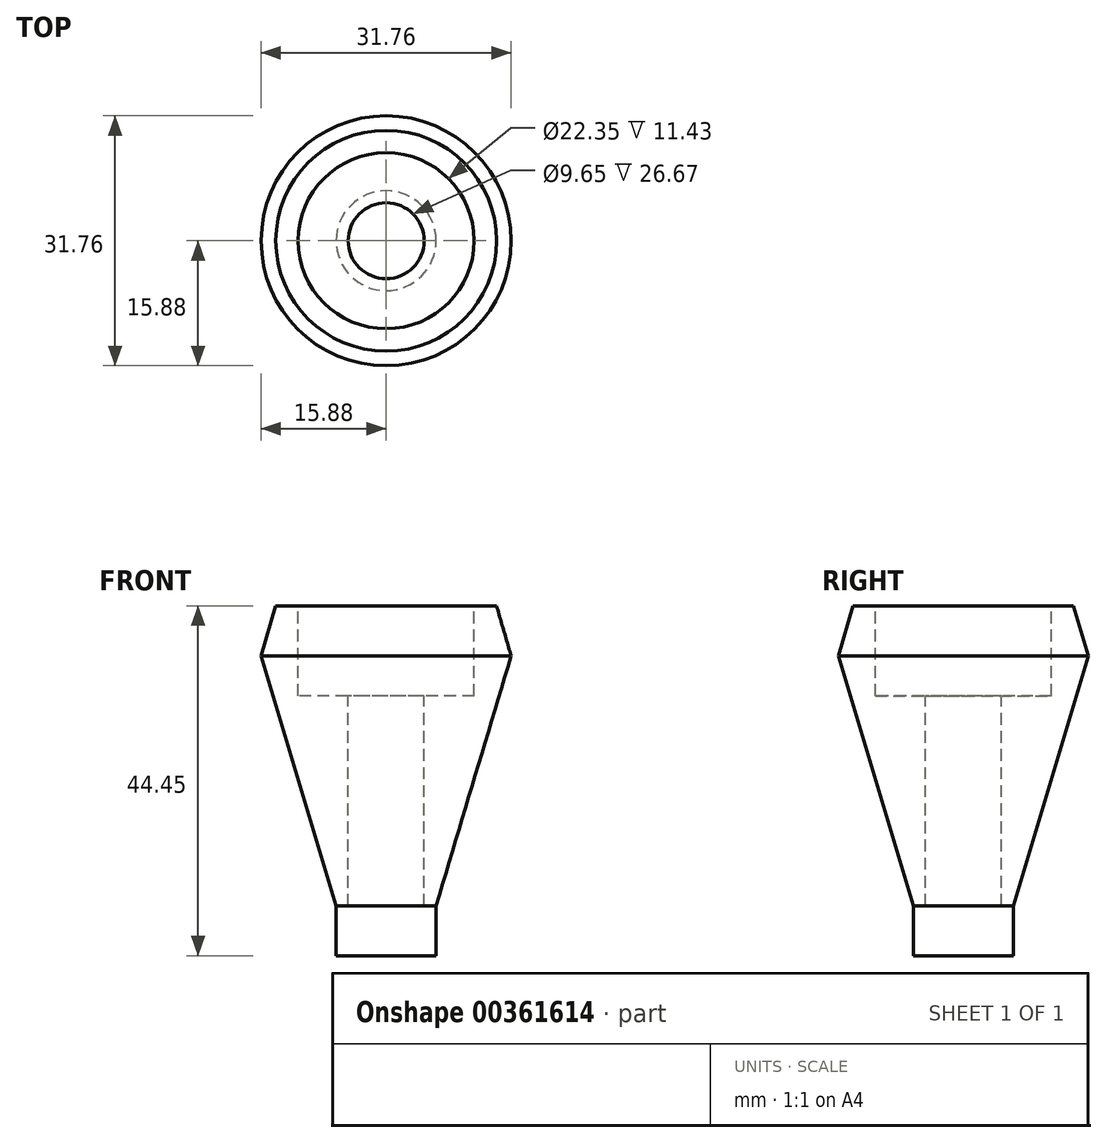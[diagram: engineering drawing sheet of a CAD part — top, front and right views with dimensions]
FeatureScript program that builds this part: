
annotation { "Feature Type Name" : "Feature", "Feature Type Description" : "" }
export const myFeature = defineFeature(function(context is Context, id is Id, definition is map)
    precondition{}
    {
        {
            var Q0;
            Q0=qCreatedBy(makeId("Front.planeOp"),FACE);
            var sketch = newSketch(context, id + "F0", { "sketchPlane" : qUnion([Q0])});
            skLineSegment(sketch, "E0", {"start": v(0, 0) * mm, "end": v(6.35, 0) * mm});
            skLineSegment(sketch, "E1", {"start": v(6.35, 0) * mm, "end": v(15.87, 31.75) * mm});
            skLineSegment(sketch, "E2", {"start": v(15.88, 31.75) * mm, "end": v(14.02, 38.1) * mm});
            skLineSegment(sketch, "E3", {"start": v(14.02, 38.1) * mm, "end": v(0, 38.1) * mm});
            skLineSegment(sketch, "E4", {"start": v(0, 38.1) * mm, "end": v(0, 0) * mm});
            skLineSegment(sketch, "E5", {"start": v(6.35, 0) * mm, "end": v(6.35, -6.35) * mm});
            skLineSegment(sketch, "E6", {"start": v(6.35, -6.35) * mm, "end": v(0, -6.35) * mm});
            skLineSegment(sketch, "E7", {"start": v(0, -6.35) * mm, "end": v(0, 0) * mm});
            skSolve(sketch);
        }
        {
            var Q0;
            Q0 = qSketchRegion(id + "F0", true);
            var Q1;
            Q1=sQuery(id+"F0.wireOp",EDGE,"E4");
            revolve(context, id + "F1", {"entities" : qUnion([Q0]), "axis" : qUnion([Q1]), "revolveType" : RevolveType.FULL});
        }
        {
            var Q0;
            Q0=makeQuery(id+"F1.opRevolve","SWEPT_FACE",FACE,{"disambiguationData":[OSD([sQuery(id+"F0.wireOp",EDGE,"E3")])]});
            var sketch = newSketch(context, id + "F2", { "sketchPlane" : qUnion([Q0])});
            skCircle(sketch, "E8", {"center": v(0, 0) * mm, "radius": 11.18 * mm});
            skSolve(sketch);
        }
        {
            var Q0;
            Q0=makeQuery(id+"F2.imprint","IMPRINT",FACE,{"disambiguationData":[TD([[makeQuery(id+"F2.imprint","IMPRINT",EDGE,{"derivedFrom":sQuery(id+"F2.wireOp",EDGE,"E8")}),1.0]])]});
            extrude(context, id + "F3", {"entities" : qUnion([Q0]), "operationType" : NewBodyOperationType.REMOVE, "oppositeDirection" : true, "depth" : 11.43 * mm});
        }
        {
            var Q0;
            Q0=makeQuery(id+"F1.opRevolve","SWEPT_FACE",FACE,{"disambiguationData":[OSD([sQuery(id+"F0.wireOp",EDGE,"E3")])]});
            var sketch = newSketch(context, id + "F4", { "sketchPlane" : qUnion([Q0])});
            skCircle(sketch, "E9", {"center": v(0, 0) * mm, "radius": 4.83 * mm});
            skSolve(sketch);
        }
        {
            var Q0;
            Q0=makeQuery(id+"F4.imprint","IMPRINT",FACE,{"disambiguationData":[TD([[makeQuery(id+"F4.imprint","IMPRINT",EDGE,{"derivedFrom":sQuery(id+"F4.wireOp",EDGE,"E9")}),1.0]])]});
            extrude(context, id + "F5", {"entities" : qUnion([Q0]), "operationType" : NewBodyOperationType.REMOVE, "oppositeDirection" : true, "depth" : 38.1 * mm});
        }
    });
